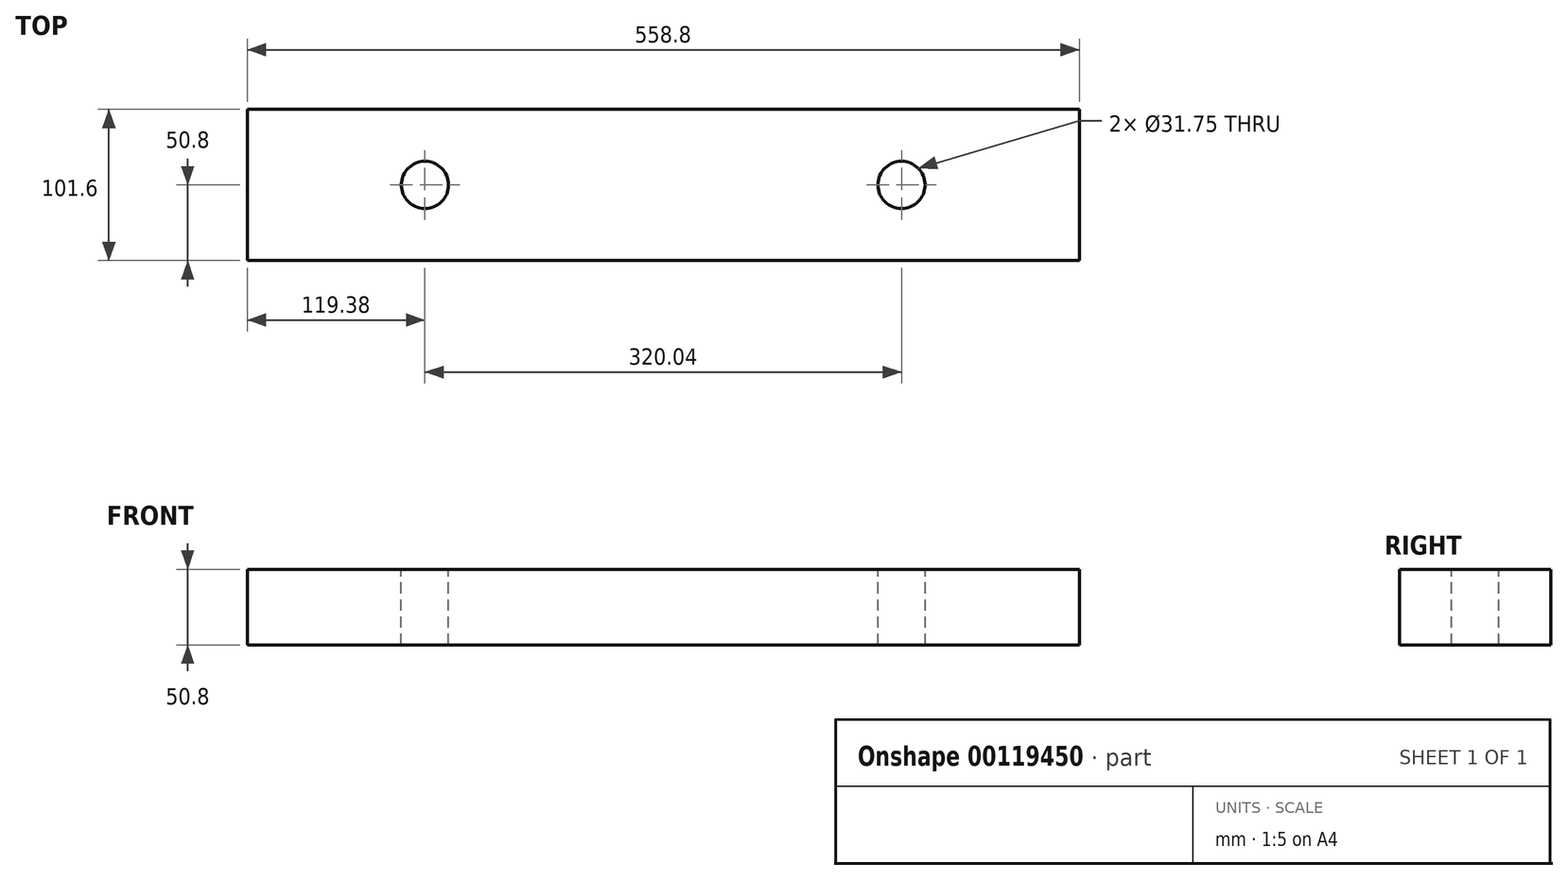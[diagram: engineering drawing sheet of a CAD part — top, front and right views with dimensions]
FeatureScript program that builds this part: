
annotation { "Feature Type Name" : "Feature", "Feature Type Description" : "" }
export const myFeature = defineFeature(function(context is Context, id is Id, definition is map)
    precondition{}
    {
        {
            var Q0;
            Q0=qCreatedBy(makeId("Top.planeOp"),FACE);
            var sketch = newSketch(context, id + "F0", { "sketchPlane" : qUnion([Q0])});
            skLineSegment(sketch, "E0.bottom", {"start": v(279.4, -50.8) * mm, "end": v(-279.4, -50.8) * mm});
            skLineSegment(sketch, "E0.top", {"start": v(279.4, 50.8) * mm, "end": v(-279.4, 50.8) * mm});
            skLineSegment(sketch, "E0.left", {"start": v(279.4, -50.8) * mm, "end": v(279.4, 50.8) * mm});
            skLineSegment(sketch, "E0.right", {"start": v(-279.4, -50.8) * mm, "end": v(-279.4, 50.8) * mm});
            skPoint(sketch, "E0.middle", {"position": v(0, 0) * mm});
            skSolve(sketch);
        }
        {
            var Q0;
            Q0 = qSketchRegion(id + "F0", true);
            extrude(context, id + "F1", {"entities" : qUnion([Q0]), "oppositeDirection" : true, "depth" : 50.8 * mm});
        }
        {
            var Q0;
            Q0=makeQuery(id+"F1.opExtrude","CAP_FACE",FACE,{"disambiguationData":[OSD([sQuery(id+"F0.wireOp",EDGE,"E0.bottom"),sQuery(id+"F0.wireOp",EDGE,"E0.top"),sQuery(id+"F0.wireOp",EDGE,"E0.left"),sQuery(id+"F0.wireOp",EDGE,"E0.right")])],"isStart":true});
            var sketch = newSketch(context, id + "F2", { "sketchPlane" : qUnion([Q0])});
            skCircle(sketch, "E1", {"center": v(-160.02, 0) * mm, "radius": 15.88 * mm});
            skCircle(sketch, "E2", {"center": v(160.02, 0) * mm, "radius": 15.88 * mm});
            skLineSegment(sketch, "E3", {"start": v(-160.02, 0) * mm, "end": v(-279.4, 0) * mm});
            skLineSegment(sketch, "E4", {"start": v(160.02, 0) * mm, "end": v(279.4, 0) * mm});
            skSolve(sketch);
        }
        {
            var Q0;
            Q0 = qSketchRegion(id + "F2", true);
            extrude(context, id + "F3", {"entities" : qUnion([Q0]), "operationType" : NewBodyOperationType.REMOVE, "endBound" : BoundingType.THROUGH_ALL, "oppositeDirection" : true, "depth" : 25.4 * mm});
        }
    });
